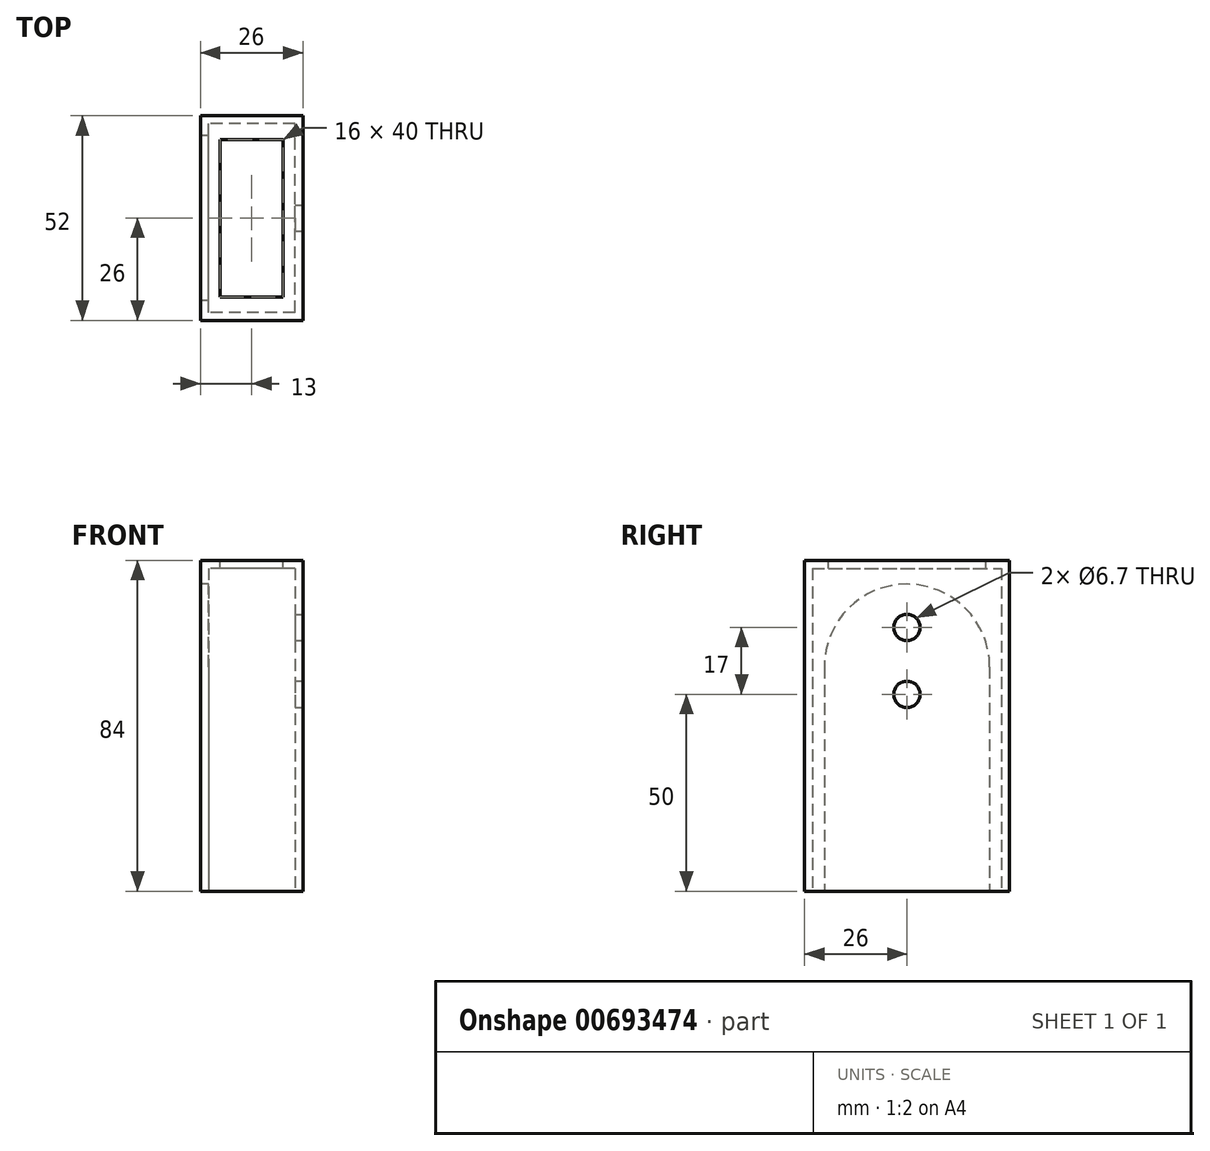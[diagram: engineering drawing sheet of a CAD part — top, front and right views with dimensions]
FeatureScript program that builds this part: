
annotation { "Feature Type Name" : "Feature", "Feature Type Description" : "" }
export const myFeature = defineFeature(function(context is Context, id is Id, definition is map)
    precondition{}
    {
        {
            var Q0;
            Q0=qCreatedBy(makeId("Top.planeOp"),FACE);
            var sketch = newSketch(context, id + "F0", { "sketchPlane" : qUnion([Q0])});
            skLineSegment(sketch, "E0.bottom", {"start": v(13, -26) * mm, "end": v(-13, -26) * mm});
            skLineSegment(sketch, "E0.top", {"start": v(13, 26) * mm, "end": v(-13, 26) * mm});
            skLineSegment(sketch, "E0.left", {"start": v(13, -26) * mm, "end": v(13, 26) * mm});
            skLineSegment(sketch, "E0.right", {"start": v(-13, -26) * mm, "end": v(-13, 26) * mm});
            skPoint(sketch, "E0.middle", {"position": v(0, 0) * mm});
            skSolve(sketch);
        }
        {
            var Q0;
            Q0 = qSketchRegion(id + "F0", true);
            extrude(context, id + "F1", {"entities" : qUnion([Q0]), "depth" : 84 * mm, "offsetDistance" : 25 * mm});
        }
        {
            var Q0;
            Q0=makeQuery(id+"F1.opExtrude","CAP_FACE",FACE,{"disambiguationData":[OSD([sQuery(id+"F0.wireOp",EDGE,"E0.bottom"),sQuery(id+"F0.wireOp",EDGE,"E0.top"),sQuery(id+"F0.wireOp",EDGE,"E0.left"),sQuery(id+"F0.wireOp",EDGE,"E0.right")])],"isStart":true});
            shell(context, id + "F2", {"entities" : qUnion([Q0]), "thickness" : 2 * mm});
        }
        {
            var Q0;
            Q0=makeQuery(id+"F1.opExtrude","SWEPT_FACE",FACE,{"disambiguationData":[OSD([sQuery(id+"F0.wireOp",EDGE,"E0.right")])]});
            var sketch = newSketch(context, id + "F3", { "sketchPlane" : qUnion([Q0])});
            skLineSegment(sketch, "E1", {"start": v(0, 0) * mm, "end": v(0, 84) * mm, "construction": true});
            skPoint(sketch, "E2", {"position": v(0, 57) * mm});
            skCircle(sketch, "E3", {"center": v(0, 57) * mm, "radius": 21 * mm});
            skLineSegment(sketch, "E4", {"start": v(-21, 57) * mm, "end": v(-21, 0) * mm});
            skLineSegment(sketch, "E5", {"start": v(21, 57) * mm, "end": v(21, 0) * mm});
            skSolve(sketch);
        }
        {
            var Q0;
            Q0 = qSketchRegion(id + "F3", true);
            var Q1;
            {var subQ0=sQuery(id+"F3.wireOp",EDGE,"E4");Q1=makeQuery(id+"F3.imprint","IMPRINT",FACE,{"disambiguationData":[TD([[makeQuery(id+"F3.imprint","IMPRINT",EDGE,{"derivedFrom":subQ0}),1.0]])]});}
            var Q2;
            {var subQ0=sQuery(id+"F3.wireOp",EDGE,"E5");Q2=makeQuery(id+"F3.imprint","IMPRINT",FACE,{"disambiguationData":[TD([[makeQuery(id+"F3.imprint","IMPRINT",EDGE,{"derivedFrom":subQ0}),-1.0]])]});}
            extrude(context, id + "F4", {"entities" : qUnion([Q0, Q1, Q2]), "operationType" : NewBodyOperationType.REMOVE, "oppositeDirection" : true, "depth" : 3 * mm, "offsetDistance" : 25 * mm});
        }
        {
            var Q0;
            Q0=makeQuery(id+"F1.opExtrude","SWEPT_FACE",FACE,{"disambiguationData":[OSD([sQuery(id+"F0.wireOp",EDGE,"E0.left")])]});
            var sketch = newSketch(context, id + "F5", { "sketchPlane" : qUnion([Q0])});
            skLineSegment(sketch, "E6", {"start": v(0, 0) * mm, "end": v(0, 84) * mm, "construction": true});
            skPoint(sketch, "E7", {"position": v(0, 67) * mm});
            skPoint(sketch, "E8", {"position": v(0, 50) * mm});
            skCircle(sketch, "E9", {"center": v(0, 67) * mm, "radius": 3.35 * mm});
            skCircle(sketch, "E10", {"center": v(0, 50) * mm, "radius": 3.35 * mm});
            skSolve(sketch);
        }
        {
            var Q0;
            Q0 = qSketchRegion(id + "F5", true);
            extrude(context, id + "F6", {"entities" : qUnion([Q0]), "operationType" : NewBodyOperationType.REMOVE, "oppositeDirection" : true, "depth" : 3 * mm, "offsetDistance" : 25 * mm});
        }
        {
            var Q0;
            Q0=makeQuery(id+"F1.opExtrude","SWEPT_FACE",FACE,{"disambiguationData":[OSD([sQuery(id+"F0.wireOp",EDGE,"E0.right")])]});
            var sketch = newSketch(context, id + "F7", { "sketchPlane" : qUnion([Q0])});
            skLineSegment(sketch, "E11", {"start": v(0, 84) * mm, "end": v(0, 0) * mm, "construction": true});
            skPoint(sketch, "E12", {"position": v(0, 67) * mm});
            skPoint(sketch, "E13", {"position": v(0, 50) * mm});
            skLineSegment(sketch, "E14.bottom", {"start": v(6.5, 60.5) * mm, "end": v(-6.5, 60.5) * mm});
            skLineSegment(sketch, "E14.top", {"start": v(6.5, 73.5) * mm, "end": v(-6.5, 73.5) * mm});
            skLineSegment(sketch, "E14.left", {"start": v(6.5, 60.5) * mm, "end": v(6.5, 73.5) * mm});
            skLineSegment(sketch, "E14.right", {"start": v(-6.5, 60.5) * mm, "end": v(-6.5, 73.5) * mm});
            skLineSegment(sketch, "E15.bottom", {"start": v(6.5, 43.5) * mm, "end": v(-6.5, 43.5) * mm});
            skLineSegment(sketch, "E15.top", {"start": v(6.5, 56.5) * mm, "end": v(-6.5, 56.5) * mm});
            skLineSegment(sketch, "E15.left", {"start": v(6.5, 43.5) * mm, "end": v(6.5, 56.5) * mm});
            skLineSegment(sketch, "E15.right", {"start": v(-6.5, 43.5) * mm, "end": v(-6.5, 56.5) * mm});
            skSolve(sketch);
        }
        {
            var Q0;
            Q0 = qSketchRegion(id + "F7", true);
            extrude(context, id + "F8", {"entities" : qUnion([Q0]), "operationType" : NewBodyOperationType.REMOVE, "oppositeDirection" : true, "depth" : 3 * mm, "offsetDistance" : 25 * mm});
        }
        {
            var Q0;
            Q0=makeQuery(id+"F1.opExtrude","CAP_FACE",FACE,{"disambiguationData":[OSD([sQuery(id+"F0.wireOp",EDGE,"E0.bottom"),sQuery(id+"F0.wireOp",EDGE,"E0.top"),sQuery(id+"F0.wireOp",EDGE,"E0.left"),sQuery(id+"F0.wireOp",EDGE,"E0.right")])],"isStart":false});
            var sketch = newSketch(context, id + "F9", { "sketchPlane" : qUnion([Q0])});
            skLineSegment(sketch, "E16.bottom", {"start": v(8, -20) * mm, "end": v(-8, -20) * mm});
            skLineSegment(sketch, "E16.top", {"start": v(8, 20) * mm, "end": v(-8, 20) * mm});
            skLineSegment(sketch, "E16.left", {"start": v(8, -20) * mm, "end": v(8, 20) * mm});
            skLineSegment(sketch, "E16.right", {"start": v(-8, -20) * mm, "end": v(-8, 20) * mm});
            skPoint(sketch, "E16.middle", {"position": v(0, 0) * mm});
            skSolve(sketch);
        }
        {
            var Q0;
            Q0 = qSketchRegion(id + "F9", true);
            extrude(context, id + "F10", {"entities" : qUnion([Q0]), "operationType" : NewBodyOperationType.REMOVE, "oppositeDirection" : true, "depth" : 25 * mm, "offsetDistance" : 25 * mm});
        }
    });
